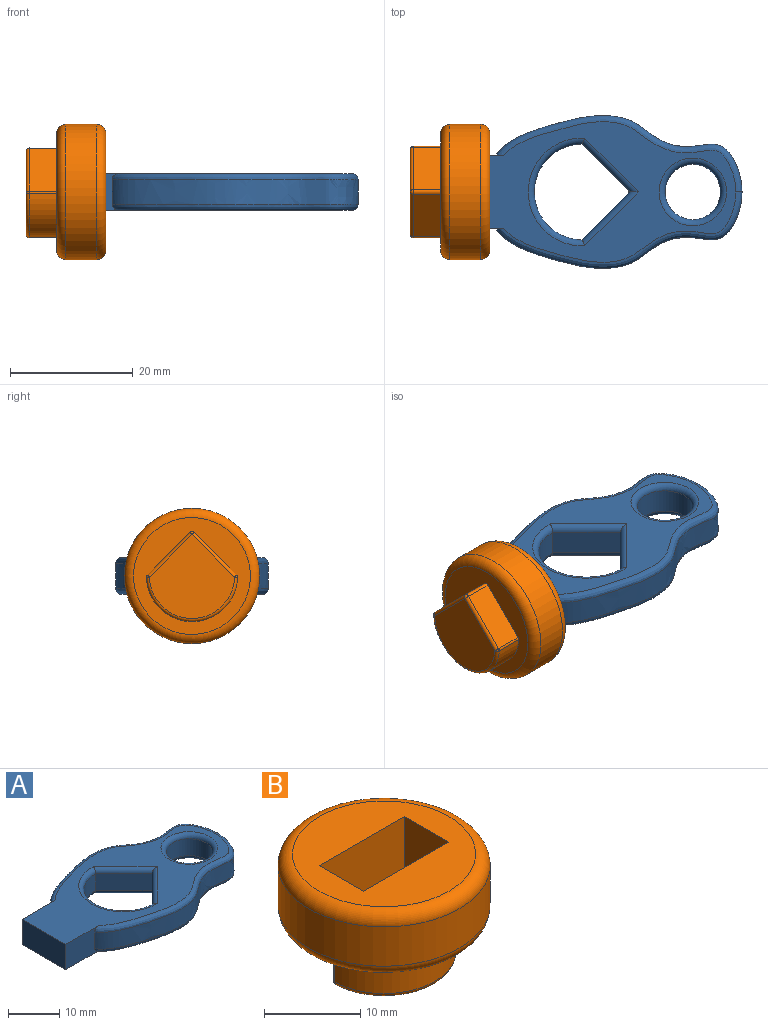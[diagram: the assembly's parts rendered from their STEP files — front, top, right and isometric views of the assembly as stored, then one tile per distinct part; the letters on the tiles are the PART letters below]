
ASSEMBLY  parts=2 mates=1
PART A: 23 faces, bbox 48.4x25.2x6.4 mm
  f0: plane 12x6mm, normal (-1,0,0), area 72mm2, adj f1,f8,f9,f10
  f1: plane 9.62x6.37mm, normal (0,-1,0), area 48.5mm2, adj f0,f2,f9,f10,f11,f17
  f2: extruded ~40x12.43mm, area 192.2mm2, adj f1,f3,f11,f17
  f3: extruded ~40x12.43mm, area 192.2mm2, adj f2,f8,f12,f18
  f4: cylinder r=7.78mm len=15.56mm, axis (0,0,-1), area 97.7mm2, adj f5,f7,f14,f20
  f5: plane 7.78x7.78mm, normal (-0.71,-0.71,0), area 44mm2, adj f4,f7,f15,f21
  f6: cylinder r=4.5mm len=9mm, axis (0,0,-1), area 113.1mm2, adj f13,f19
  f7: plane 7.78x7.78mm, normal (-0.71,0.71,0), area 44mm2, adj f4,f5,f16,f22
  f8: plane 9.62x6.37mm, normal (0,1,0), area 48.5mm2, adj f0,f3,f9,f10,f12,f18
  f9: plane 47x22.86mm, normal (0,0,1), area 459.3mm2, adj f0,f1,f8,f17,f18,f19,f20,f21
  f10: plane 47x22.86mm, normal (0,0,-1), area 459.3mm2, adj f0,f1,f8,f11,f12,f13,f14,f15
  f11: bspline ~40.69x12.66mm, area 73.4mm2, adj f1,f2,f10,f12
  f12: bspline ~40.69x12.66mm, area 73.4mm2, adj f3,f8,f10,f11
  f13: torus R=5.5mm, axis (0,0,1), area 48mm2, adj f6,f10
  f14: torus R=8.78mm, axis (0,0,1), area 40.8mm2, adj f4,f10,f15,f16
  f15: cylinder r=1mm len=9.48mm, axis (0.71,-0.71,0), area 18.4mm2, adj f5,f10,f14,f16
  f16: cylinder r=1mm len=9.48mm, axis (-0.71,-0.71,0), area 18.4mm2, adj f7,f10,f14,f15
  f17: bspline ~40.69x12.66mm, area 73.4mm2, adj f1,f2,f9,f18
  f18: bspline ~40.69x12.66mm, area 73.4mm2, adj f3,f8,f9,f17
  f19: torus R=5.5mm, axis (0,0,1), area 48mm2, adj f6,f9
  f20: torus R=8.78mm, axis (0,0,1), area 40.8mm2, adj f4,f9,f21,f22
  f21: cylinder r=1mm len=9.48mm, axis (-0.71,0.71,0), area 18.4mm2, adj f5,f9,f20,f22
  f22: cylinder r=1mm len=9.48mm, axis (0.71,0.71,0), area 18.4mm2, adj f7,f9,f20,f21
PART B: 23 faces, bbox 23.8x23.8x13 mm
  f0: plane 19x19mm, normal (0,0,1), area 202.3mm2, adj f3,f4,f5,f6,f9
  f1: cylinder r=11mm len=22mm, axis (0,0,-1), area 345.6mm2, adj f8,f9
  f2: plane 19x19mm, normal (0,0,-1), area 141.9mm2, adj f8,f10,f11,f12,f14,f16,f22
  f3: plane 7x6.5mm, normal (-1,0,0), area 45.5mm2, adj f0,f4,f6,f7
  f4: plane 12.5x7mm, normal (0,-1,0), area 87.5mm2, adj f0,f3,f5,f7
  f5: plane 7x6.5mm, normal (1,0,0), area 45.5mm2, adj f0,f4,f6,f7
  f6: plane 12.5x7mm, normal (0,1,0), area 87.5mm2, adj f0,f3,f5,f7
  f7: plane 12.5x6.5mm, normal (0,0,1), area 81.2mm2, adj f3,f4,f5,f6
  f8: torus R=9.5mm, axis (0,0,1), area 154.8mm2, adj f1,f2
  f9: torus R=9.5mm, axis (0,0,1), area 154.8mm2, adj f0,f1
  f10: cylinder r=7.42mm len=14.84mm, axis (0,0,1), area 103mm2, adj f2,f14,f19,f22
  f11: plane 6.92x6.92mm, normal (0.71,0.71,0), area 44mm2, adj f2,f14,f15,f16
  f12: plane 6.92x6.92mm, normal (-0.71,0.71,0), area 44mm2, adj f2,f16,f20,f22
  f13: plane 13.84x13.64mm, normal (0,0,-1), area 120.4mm2, adj f15,f19,f20
  f14: cylinder r=0.5mm len=4.5mm, axis (0,0,1), area 1.8mm2, adj f2,f10,f11,f17
  f15: cylinder r=0.5mm len=7.28mm, axis (0.71,-0.71,0), area 7.7mm2, adj f11,f13,f17,f18
  f16: cylinder r=0.5mm len=4.5mm, axis (0,0,1), area 3.5mm2, adj f2,f11,f12,f18
  f17: sphere r=0.5mm, area 0.2mm2, adj f14,f15,f19
  f18: sphere r=0.5mm, area 0.4mm2, adj f15,f16,f20
  f19: torus R=6.92mm, axis (0,0,1), area 17.5mm2, adj f10,f13,f17,f21
  f20: cylinder r=0.5mm len=7.28mm, axis (0.71,0.71,0), area 7.7mm2, adj f12,f13,f18,f21
  f21: sphere r=0.5mm, area 0.2mm2, adj f19,f20,f22
  f22: cylinder r=0.5mm len=4.5mm, axis (0,0,1), area 1.8mm2, adj f2,f10,f12,f21
PLACE A t=(-19.23,2.66,-3.68)mm fixed
PLACE B rot(axis=(0.58,0.58,0.58),120deg) t=(-20.23,2.66,-0.68)mm
MATE fastened A.f0 <-> B.f10  axis (-1,0,0) through (-19.23,2.66,-0.68)mm
